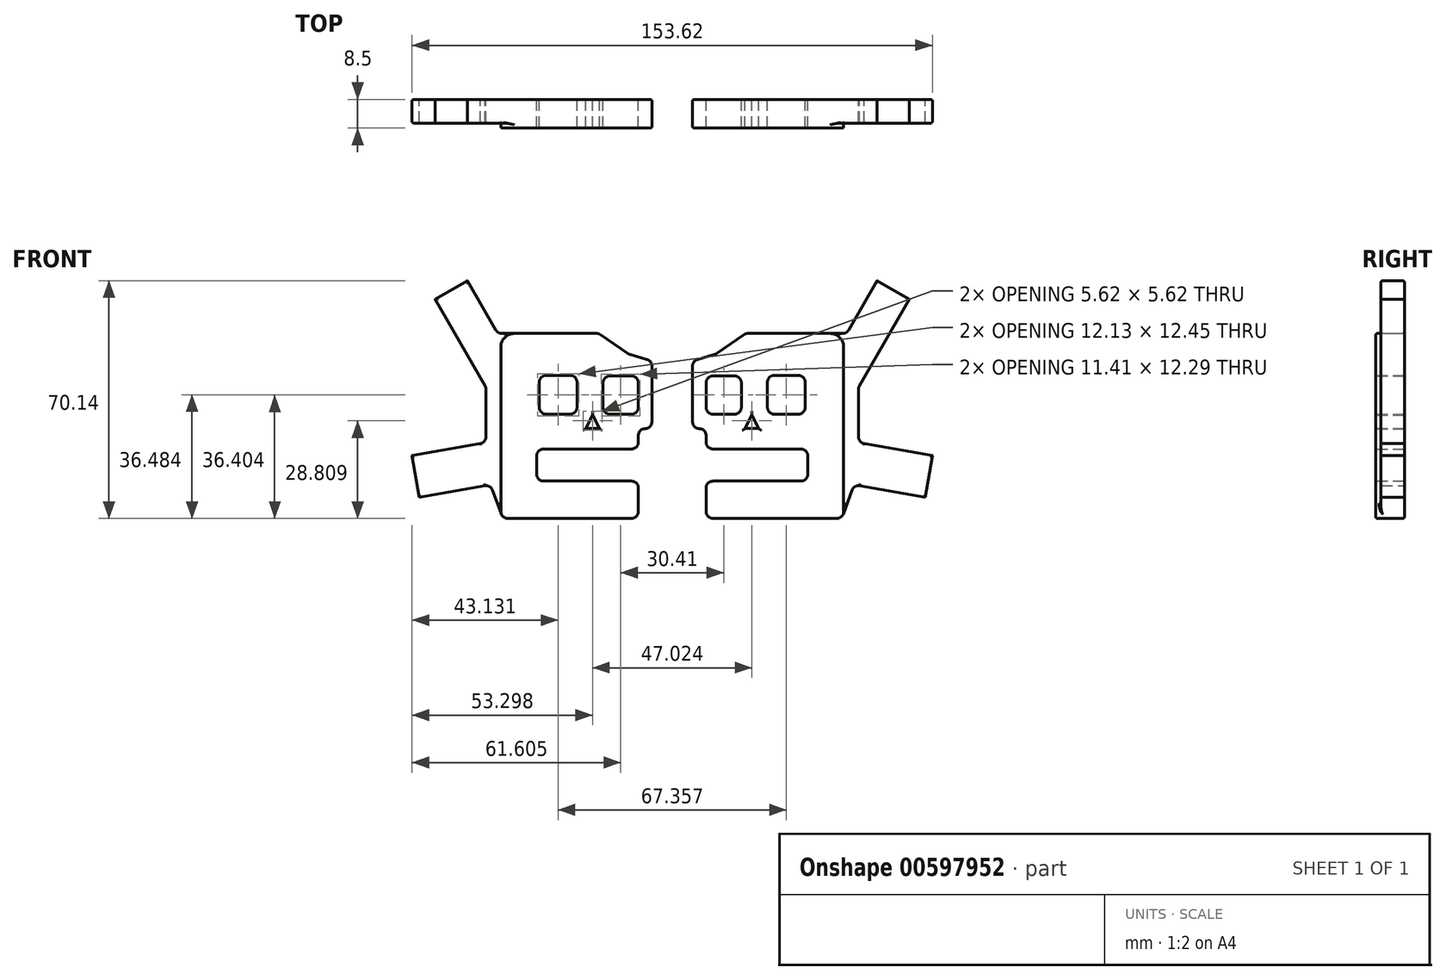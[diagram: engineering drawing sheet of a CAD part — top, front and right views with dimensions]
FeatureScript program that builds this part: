
annotation { "Feature Type Name" : "Feature", "Feature Type Description" : "" }
export const myFeature = defineFeature(function(context is Context, id is Id, definition is map)
    precondition{}
    {
        {
            var Q0;
            Q0=qCreatedBy(makeId("Front.planeOp"),FACE);
            var sketch = newSketch(context, id + "F0", { "sketchPlane" : qUnion([Q0])});
            skLineSegment(sketch, "E0", {"start": v(2, 0) * mm, "end": v(28, 0) * mm});
            skLineSegment(sketch, "E1", {"start": v(30, 2) * mm, "end": v(30, 7.5) * mm});
            skLineSegment(sketch, "E2", {"start": v(28, 9.5) * mm, "end": v(2, 9.5) * mm});
            skPoint(sketch, "E3.visualSharp", {"position": v(30, 9.5) * mm});
            skArc(sketch, "E3.filletArc", {"start": v(30, 7.5) * mm, "mid": v(29.41, 8.91) * mm, "end": v(28, 9.5) * mm});
            skPoint(sketch, "E4.visualSharp", {"position": v(30, 0) * mm});
            skArc(sketch, "E4.filletArc", {"start": v(28, 0) * mm, "mid": v(29.41, 0.59) * mm, "end": v(30, 2) * mm});
            skLineSegment(sketch, "E5", {"start": v(0, -2) * mm, "end": v(0, -9) * mm});
            skLineSegment(sketch, "E6", {"start": v(2, -11) * mm, "end": v(38.6, -11) * mm});
            skLineSegment(sketch, "E7", {"start": v(40.48, -9.68) * mm, "end": v(43.04, -2.66) * mm});
            skLineSegment(sketch, "E8", {"start": v(45, 13.04) * mm, "end": v(45, 27.12) * mm});
            skLineSegment(sketch, "E9", {"start": v(45.27, 28.12) * mm, "end": v(60, 53.64) * mm});
            skLineSegment(sketch, "E10", {"start": v(60, 53.64) * mm, "end": v(50.47, 59.14) * mm});
            skLineSegment(sketch, "E11", {"start": v(50.47, 59.14) * mm, "end": v(42.06, 44.57) * mm});
            skLineSegment(sketch, "E12", {"start": v(40.33, 43.57) * mm, "end": v(12.31, 43.57) * mm});
            skLineSegment(sketch, "E13", {"start": v(11.18, 43.22) * mm, "end": v(3.06, 37.63) * mm});
            skLineSegment(sketch, "E14", {"start": v(2.48, 37.35) * mm, "end": v(-2.55, 35.9) * mm});
            skLineSegment(sketch, "E15", {"start": v(-4, 33.98) * mm, "end": v(-4, 17.49) * mm});
            skLineSegment(sketch, "E16", {"start": v(-2, 15.49) * mm, "end": v(-2, 15.49) * mm});
            skPoint(sketch, "E17.end.orphan", {"position": v(0.1, 9.49) * mm});
            skLineSegment(sketch, "E18", {"start": v(0, 11.5) * mm, "end": v(0, 13.49) * mm});
            skPoint(sketch, "E19.orphan", {"position": v(0.1, 15.49) * mm});
            skLineSegment(sketch, "E20.bottom", {"start": v(2, 19.76) * mm, "end": v(8.41, 19.76) * mm});
            skLineSegment(sketch, "E20.top", {"start": v(2, 31.05) * mm, "end": v(8.41, 31.05) * mm});
            skLineSegment(sketch, "E20.left", {"start": v(0, 21.76) * mm, "end": v(0, 29.05) * mm});
            skLineSegment(sketch, "E20.right", {"start": v(10.41, 21.76) * mm, "end": v(10.41, 29.05) * mm});
            skLineSegment(sketch, "E21.bottom", {"start": v(20.12, 19.76) * mm, "end": v(27.24, 19.76) * mm});
            skLineSegment(sketch, "E21.top", {"start": v(20.12, 31.21) * mm, "end": v(27.24, 31.21) * mm});
            skLineSegment(sketch, "E21.left", {"start": v(18.12, 21.76) * mm, "end": v(18.12, 29.21) * mm});
            skLineSegment(sketch, "E21.right", {"start": v(29.24, 21.76) * mm, "end": v(29.24, 29.21) * mm});
            skLineSegment(sketch, "E22", {"start": v(13.48, 19.5) * mm, "end": v(11.5, 15.5) * mm});
            skLineSegment(sketch, "E23", {"start": v(11.5, 15.5) * mm, "end": v(15.5, 15.5) * mm});
            skLineSegment(sketch, "E24", {"start": v(15.5, 15.5) * mm, "end": v(13.48, 19.5) * mm});
            skPoint(sketch, "E25.visualSharp", {"position": v(29.24, 19.76) * mm});
            skArc(sketch, "E25.filletArc", {"start": v(27.24, 19.76) * mm, "mid": v(28.66, 20.34) * mm, "end": v(29.24, 21.76) * mm});
            skPoint(sketch, "E26.visualSharp", {"position": v(18.12, 19.76) * mm});
            skArc(sketch, "E26.filletArc", {"start": v(18.12, 21.76) * mm, "mid": v(18.7, 20.34) * mm, "end": v(20.12, 19.76) * mm});
            skPoint(sketch, "E27.visualSharp", {"position": v(29.24, 31.21) * mm});
            skArc(sketch, "E27.filletArc", {"start": v(29.24, 29.21) * mm, "mid": v(28.66, 30.62) * mm, "end": v(27.24, 31.21) * mm});
            skPoint(sketch, "E28.visualSharp", {"position": v(18.12, 31.21) * mm});
            skArc(sketch, "E28.filletArc", {"start": v(20.12, 31.21) * mm, "mid": v(18.7, 30.62) * mm, "end": v(18.12, 29.21) * mm});
            skPoint(sketch, "E29.visualSharp", {"position": v(10.41, 31.05) * mm});
            skArc(sketch, "E29.filletArc", {"start": v(10.41, 29.05) * mm, "mid": v(9.82, 30.46) * mm, "end": v(8.41, 31.05) * mm});
            skPoint(sketch, "E30.visualSharp", {"position": v(10.41, 19.76) * mm});
            skArc(sketch, "E30.filletArc", {"start": v(8.41, 19.76) * mm, "mid": v(9.82, 20.34) * mm, "end": v(10.41, 21.76) * mm});
            skPoint(sketch, "E31.visualSharp", {"position": v(0, 19.76) * mm});
            skArc(sketch, "E31.filletArc", {"start": v(0, 21.76) * mm, "mid": v(0.59, 20.34) * mm, "end": v(2, 19.76) * mm});
            skPoint(sketch, "E32.visualSharp", {"position": v(0, 31.05) * mm});
            skArc(sketch, "E32.filletArc", {"start": v(2, 31.05) * mm, "mid": v(0.59, 30.46) * mm, "end": v(0, 29.05) * mm});
            skPoint(sketch, "E33.visualSharp", {"position": v(-4, 15.49) * mm});
            skArc(sketch, "E33.filletArc", {"start": v(-4, 17.49) * mm, "mid": v(-3.41, 16.07) * mm, "end": v(-2, 15.49) * mm});
            skPoint(sketch, "E34.visualSharp", {"position": v(0, 15.49) * mm});
            skArc(sketch, "E34.filletArc", {"start": v(0, 13.49) * mm, "mid": v(-0.59, 14.9) * mm, "end": v(-2, 15.49) * mm});
            skPoint(sketch, "E35.visualSharp", {"position": v(-4, 35.49) * mm});
            skArc(sketch, "E35.filletArc", {"start": v(-2.55, 35.9) * mm, "mid": v(-3.6, 35.18) * mm, "end": v(-4, 33.98) * mm});
            skPoint(sketch, "E36.visualSharp", {"position": v(2.8, 37.44) * mm});
            skArc(sketch, "E36.filletArc", {"start": v(2.48, 37.35) * mm, "mid": v(2.78, 37.46) * mm, "end": v(3.06, 37.63) * mm});
            skPoint(sketch, "E37.visualSharp", {"position": v(11.69, 43.57) * mm});
            skArc(sketch, "E37.filletArc", {"start": v(12.31, 43.57) * mm, "mid": v(11.72, 43.48) * mm, "end": v(11.18, 43.22) * mm});
            skPoint(sketch, "E38.visualSharp", {"position": v(41.49, 43.57) * mm});
            skArc(sketch, "E38.filletArc", {"start": v(40.33, 43.57) * mm, "mid": v(41.33, 43.84) * mm, "end": v(42.06, 44.57) * mm});
            skPoint(sketch, "E39.visualSharp", {"position": v(45, 27.66) * mm});
            skArc(sketch, "E39.filletArc", {"start": v(45.27, 28.12) * mm, "mid": v(45.07, 27.64) * mm, "end": v(45, 27.12) * mm});
            skPoint(sketch, "E40.visualSharp", {"position": v(45, 12.8) * mm});
            skArc(sketch, "E40.filletArc", {"start": v(45, 13.04) * mm, "mid": v(45.48, 11.74) * mm, "end": v(46.7, 11.07) * mm});
            skPoint(sketch, "E41.visualSharp", {"position": v(47.97, 10.9) * mm});
            skArc(sketch, "E41.filletArc", {"start": v(45.24, -1.37) * mm, "mid": v(43.9, -1.62) * mm, "end": v(43.04, -2.66) * mm});
            skPoint(sketch, "E42.visualSharp", {"position": v(0, 0) * mm});
            skArc(sketch, "E42.filletArc", {"start": v(2, 0) * mm, "mid": v(0.59, -0.59) * mm, "end": v(0, -2) * mm});
            skPoint(sketch, "E43.visualSharp", {"position": v(0, -11) * mm});
            skArc(sketch, "E43.filletArc", {"start": v(0, -9) * mm, "mid": v(0.59, -10.41) * mm, "end": v(2, -11) * mm});
            skPoint(sketch, "E44.visualSharp", {"position": v(0, 9.5) * mm});
            skArc(sketch, "E44.filletArc", {"start": v(0, 11.5) * mm, "mid": v(0.59, 10.09) * mm, "end": v(2, 9.5) * mm});
            skPoint(sketch, "E45.visualSharp", {"position": v(40, -11) * mm});
            skArc(sketch, "E45.filletArc", {"start": v(38.6, -11) * mm, "mid": v(39.75, -10.64) * mm, "end": v(40.48, -9.68) * mm});
            skPoint(sketch, "E46.start.orphan", {"position": v(65, 12.8) * mm});
            skLineSegment(sketch, "E47", {"start": v(46.7, 11.07) * mm, "end": v(66.81, 7.52) * mm});
            skLineSegment(sketch, "E48", {"start": v(66.81, 7.52) * mm, "end": v(64.64, -4.8) * mm});
            skLineSegment(sketch, "E49", {"start": v(45.24, -1.37) * mm, "end": v(64.64, -4.8) * mm});
            skSolve(sketch);
        }
        {
            var Q0;
            Q0=qSketchRegion(id+"F0",true);
            extrude(context, id + "F1", {"entities" : qUnion([Q0]), "depth" : 7 * mm, "offsetDistance" : 25 * mm});
        }
        {
            var Q0;
            Q0=makeQuery(id+"F1.opExtrude","CAP_FACE",FACE,{"disambiguationData":[OSD([sQuery(id+"F0.wireOp",EDGE,"E0"),sQuery(id+"F0.wireOp",EDGE,"E1"),sQuery(id+"F0.wireOp",EDGE,"E2"),sQuery(id+"F0.wireOp",EDGE,"E3.filletArc"),sQuery(id+"F0.wireOp",EDGE,"E4.filletArc"),sQuery(id+"F0.wireOp",EDGE,"E5"),sQuery(id+"F0.wireOp",EDGE,"E6"),sQuery(id+"F0.wireOp",EDGE,"E7"),sQuery(id+"F0.wireOp",EDGE,"E8"),sQuery(id+"F0.wireOp",EDGE,"E9"),sQuery(id+"F0.wireOp",EDGE,"E10"),sQuery(id+"F0.wireOp",EDGE,"E11"),sQuery(id+"F0.wireOp",EDGE,"E12"),sQuery(id+"F0.wireOp",EDGE,"E13"),sQuery(id+"F0.wireOp",EDGE,"E14"),sQuery(id+"F0.wireOp",EDGE,"E15"),sQuery(id+"F0.wireOp",EDGE,"E18"),sQuery(id+"F0.wireOp",EDGE,"E20.bottom"),sQuery(id+"F0.wireOp",EDGE,"E20.top"),sQuery(id+"F0.wireOp",EDGE,"E20.left"),sQuery(id+"F0.wireOp",EDGE,"E20.right"),sQuery(id+"F0.wireOp",EDGE,"E21.bottom"),sQuery(id+"F0.wireOp",EDGE,"E21.top"),sQuery(id+"F0.wireOp",EDGE,"E21.left"),sQuery(id+"F0.wireOp",EDGE,"E21.right"),sQuery(id+"F0.wireOp",EDGE,"E22"),sQuery(id+"F0.wireOp",EDGE,"E23"),sQuery(id+"F0.wireOp",EDGE,"E24"),sQuery(id+"F0.wireOp",EDGE,"E25.filletArc"),sQuery(id+"F0.wireOp",EDGE,"E26.filletArc"),sQuery(id+"F0.wireOp",EDGE,"E27.filletArc"),sQuery(id+"F0.wireOp",EDGE,"E28.filletArc"),sQuery(id+"F0.wireOp",EDGE,"E29.filletArc"),sQuery(id+"F0.wireOp",EDGE,"E30.filletArc"),sQuery(id+"F0.wireOp",EDGE,"E31.filletArc"),sQuery(id+"F0.wireOp",EDGE,"E32.filletArc"),sQuery(id+"F0.wireOp",EDGE,"E33.filletArc"),sQuery(id+"F0.wireOp",EDGE,"E34.filletArc"),sQuery(id+"F0.wireOp",EDGE,"E35.filletArc"),sQuery(id+"F0.wireOp",EDGE,"E36.filletArc"),sQuery(id+"F0.wireOp",EDGE,"E37.filletArc"),sQuery(id+"F0.wireOp",EDGE,"E38.filletArc"),sQuery(id+"F0.wireOp",EDGE,"E39.filletArc"),sQuery(id+"F0.wireOp",EDGE,"E40.filletArc"),sQuery(id+"F0.wireOp",EDGE,"E41.filletArc"),sQuery(id+"F0.wireOp",EDGE,"E42.filletArc"),sQuery(id+"F0.wireOp",EDGE,"E43.filletArc"),sQuery(id+"F0.wireOp",EDGE,"E44.filletArc"),sQuery(id+"F0.wireOp",EDGE,"E45.filletArc"),sQuery(id+"F0.wireOp",EDGE,"E47"),sQuery(id+"F0.wireOp",EDGE,"E48"),sQuery(id+"F0.wireOp",EDGE,"E49")])],"isStart":false});
            var sketch = newSketch(context, id + "F2", { "sketchPlane" : qUnion([Q0])});
            skLineSegment(sketch, "E50.0", {"start": v(36.6, 43.57) * mm, "end": v(12.31, 43.57) * mm});
            skPoint(sketch, "E51.0", {"position": v(45, 27.12) * mm});
            skArc(sketch, "E52.0", {"start": v(12.31, 43.57) * mm, "mid": v(11.72, 43.48) * mm, "end": v(11.18, 43.22) * mm});
            skLineSegment(sketch, "E53.0", {"start": v(11.18, 43.22) * mm, "end": v(3.06, 37.63) * mm});
            skPoint(sketch, "E54.0", {"position": v(2.48, 37.35) * mm});
            skLineSegment(sketch, "E55.0", {"start": v(2.48, 37.35) * mm, "end": v(-2.55, 35.9) * mm});
            skArc(sketch, "E56.0", {"start": v(2.48, 37.35) * mm, "mid": v(2.78, 37.46) * mm, "end": v(3.06, 37.63) * mm});
            skArc(sketch, "E57.0", {"start": v(-2.55, 35.9) * mm, "mid": v(-3.6, 35.18) * mm, "end": v(-4, 33.98) * mm});
            skLineSegment(sketch, "E58.0", {"start": v(-4, 33.98) * mm, "end": v(-4, 17.49) * mm});
            skLineSegment(sketch, "E59.0", {"start": v(0, 21.76) * mm, "end": v(0, 29.05) * mm});
            skArc(sketch, "E60.0", {"start": v(2, 31.05) * mm, "mid": v(0.59, 30.46) * mm, "end": v(0, 29.05) * mm});
            skLineSegment(sketch, "E61.0", {"start": v(2, 31.05) * mm, "end": v(8.41, 31.05) * mm});
            skArc(sketch, "E62.0", {"start": v(10.41, 29.05) * mm, "mid": v(9.82, 30.46) * mm, "end": v(8.41, 31.05) * mm});
            skLineSegment(sketch, "E63.0", {"start": v(10.41, 21.76) * mm, "end": v(10.41, 29.05) * mm});
            skArc(sketch, "E64.0", {"start": v(8.41, 19.76) * mm, "mid": v(9.82, 20.34) * mm, "end": v(10.41, 21.76) * mm});
            skLineSegment(sketch, "E65.0", {"start": v(2, 19.76) * mm, "end": v(8.41, 19.76) * mm});
            skArc(sketch, "E66.0", {"start": v(0, 21.76) * mm, "mid": v(0.59, 20.34) * mm, "end": v(2, 19.76) * mm});
            skPoint(sketch, "E67.0", {"position": v(-2, 15.49) * mm});
            skArc(sketch, "E68.0", {"start": v(-4, 17.49) * mm, "mid": v(-3.41, 16.07) * mm, "end": v(-2, 15.49) * mm});
            skPoint(sketch, "E69.0", {"position": v(0, 13.49) * mm});
            skArc(sketch, "E70.0", {"start": v(0, 13.49) * mm, "mid": v(-0.59, 14.9) * mm, "end": v(-2, 15.49) * mm});
            skPoint(sketch, "E71.0", {"position": v(0, 11.5) * mm});
            skLineSegment(sketch, "E72.0", {"start": v(0, 11.5) * mm, "end": v(0, 13.49) * mm});
            skArc(sketch, "E73.0", {"start": v(0, 11.5) * mm, "mid": v(0.59, 10.09) * mm, "end": v(2, 9.5) * mm});
            skLineSegment(sketch, "E74.0", {"start": v(28, 9.5) * mm, "end": v(2, 9.5) * mm});
            skPoint(sketch, "E75.0", {"position": v(13.48, 19.5) * mm});
            skLineSegment(sketch, "E76.0", {"start": v(20.12, 19.76) * mm, "end": v(27.24, 19.76) * mm});
            skPoint(sketch, "E77.0", {"position": v(18.12, 21.76) * mm});
            skLineSegment(sketch, "E78.0", {"start": v(20.12, 31.21) * mm, "end": v(27.24, 31.21) * mm});
            skLineSegment(sketch, "E79.0", {"start": v(29.24, 21.76) * mm, "end": v(29.24, 29.21) * mm});
            skArc(sketch, "E80.0", {"start": v(29.24, 29.21) * mm, "mid": v(28.66, 30.62) * mm, "end": v(27.24, 31.21) * mm});
            skLineSegment(sketch, "E81.0", {"start": v(18.12, 21.76) * mm, "end": v(18.12, 29.21) * mm});
            skArc(sketch, "E82.0", {"start": v(18.12, 21.76) * mm, "mid": v(18.7, 20.34) * mm, "end": v(20.12, 19.76) * mm});
            skArc(sketch, "E83.0", {"start": v(20.12, 31.21) * mm, "mid": v(18.7, 30.62) * mm, "end": v(18.12, 29.21) * mm});
            skArc(sketch, "E84.0", {"start": v(27.24, 19.76) * mm, "mid": v(28.66, 20.34) * mm, "end": v(29.24, 21.76) * mm});
            skLineSegment(sketch, "E85.0", {"start": v(15.5, 15.5) * mm, "end": v(13.48, 19.5) * mm});
            skLineSegment(sketch, "E86.1", {"start": v(13.48, 19.5) * mm, "end": v(11.5, 15.5) * mm});
            skLineSegment(sketch, "E87.0", {"start": v(11.5, 15.5) * mm, "end": v(15.5, 15.5) * mm});
            skArc(sketch, "E88.0", {"start": v(30, 7.5) * mm, "mid": v(29.41, 8.91) * mm, "end": v(28, 9.5) * mm});
            skLineSegment(sketch, "E89.1", {"start": v(30, 2) * mm, "end": v(30, 7.5) * mm});
            skPoint(sketch, "E90.0", {"position": v(28, 0) * mm});
            skLineSegment(sketch, "E91.0", {"start": v(2, 0) * mm, "end": v(28, 0) * mm});
            skArc(sketch, "E92.0", {"start": v(28, 0) * mm, "mid": v(29.41, 0.59) * mm, "end": v(30, 2) * mm});
            skLineSegment(sketch, "E93.0", {"start": v(0, -2) * mm, "end": v(0, -9) * mm});
            skArc(sketch, "E94.0", {"start": v(2, 0) * mm, "mid": v(0.59, -0.59) * mm, "end": v(0, -2) * mm});
            skArc(sketch, "E95.0", {"start": v(0, -9) * mm, "mid": v(0.59, -10.41) * mm, "end": v(2, -11) * mm});
            skLineSegment(sketch, "E96.0", {"start": v(2, -11) * mm, "end": v(38.6, -11) * mm});
            skArc(sketch, "E97.0", {"start": v(38.6, -11) * mm, "mid": v(40.01, -10.41) * mm, "end": v(40.6, -9) * mm});
            skPoint(sketch, "E98.orphan", {"position": v(40.48, -9.68) * mm});
            skLineSegment(sketch, "E99", {"start": v(40.6, -9) * mm, "end": v(40.6, 39.57) * mm});
            skPoint(sketch, "E100.orphan", {"position": v(40.33, 43.57) * mm});
            skPoint(sketch, "E101.visualSharp", {"position": v(40.6, 43.57) * mm});
            skArc(sketch, "E101.filletArc", {"start": v(40.6, 39.57) * mm, "mid": v(39.43, 42.4) * mm, "end": v(36.6, 43.57) * mm});
            skSolve(sketch);
        }
        {
            var Q0;
            Q0=makeQuery(id+"F2.imprint","IMPRINT",FACE,{"disambiguationData":[TD([[makeQuery(id+"F2.imprint","IMPRINT",EDGE,{"derivedFrom":sQuery(id+"F2.wireOp",EDGE,"E50.0")}),1.0]])]});
            extrude(context, id + "F3", {"entities" : qUnion([Q0]), "operationType" : NewBodyOperationType.ADD, "depth" : 1.5 * mm, "offsetDistance" : 25 * mm});
        }
        {
            var Q0;
            Q0=makeQuery(id+"F3.opExtrude","CAP_FACE",FACE,{"disambiguationData":[OSD([sQuery(id+"F2.wireOp",EDGE,"E50.0"),sQuery(id+"F2.wireOp",EDGE,"E52.0"),sQuery(id+"F2.wireOp",EDGE,"E53.0"),sQuery(id+"F2.wireOp",EDGE,"E55.0"),sQuery(id+"F2.wireOp",EDGE,"E56.0"),sQuery(id+"F2.wireOp",EDGE,"E57.0"),sQuery(id+"F2.wireOp",EDGE,"E58.0"),sQuery(id+"F2.wireOp",EDGE,"E59.0"),sQuery(id+"F2.wireOp",EDGE,"E60.0"),sQuery(id+"F2.wireOp",EDGE,"E61.0"),sQuery(id+"F2.wireOp",EDGE,"E62.0"),sQuery(id+"F2.wireOp",EDGE,"E63.0"),sQuery(id+"F2.wireOp",EDGE,"E64.0"),sQuery(id+"F2.wireOp",EDGE,"E65.0"),sQuery(id+"F2.wireOp",EDGE,"E66.0"),sQuery(id+"F2.wireOp",EDGE,"E68.0"),sQuery(id+"F2.wireOp",EDGE,"E70.0"),sQuery(id+"F2.wireOp",EDGE,"E72.0"),sQuery(id+"F2.wireOp",EDGE,"E73.0"),sQuery(id+"F2.wireOp",EDGE,"E74.0"),sQuery(id+"F2.wireOp",EDGE,"E76.0"),sQuery(id+"F2.wireOp",EDGE,"E78.0"),sQuery(id+"F2.wireOp",EDGE,"E79.0"),sQuery(id+"F2.wireOp",EDGE,"E80.0"),sQuery(id+"F2.wireOp",EDGE,"E81.0"),sQuery(id+"F2.wireOp",EDGE,"E82.0"),sQuery(id+"F2.wireOp",EDGE,"E83.0"),sQuery(id+"F2.wireOp",EDGE,"E84.0"),sQuery(id+"F2.wireOp",EDGE,"E85.0"),sQuery(id+"F2.wireOp",EDGE,"E86.1"),sQuery(id+"F2.wireOp",EDGE,"E87.0"),sQuery(id+"F2.wireOp",EDGE,"E88.0"),sQuery(id+"F2.wireOp",EDGE,"E89.1"),sQuery(id+"F2.wireOp",EDGE,"E91.0"),sQuery(id+"F2.wireOp",EDGE,"E92.0"),sQuery(id+"F2.wireOp",EDGE,"E93.0"),sQuery(id+"F2.wireOp",EDGE,"E94.0"),sQuery(id+"F2.wireOp",EDGE,"E95.0"),sQuery(id+"F2.wireOp",EDGE,"E96.0"),sQuery(id+"F2.wireOp",EDGE,"E97.0"),sQuery(id+"F2.wireOp",EDGE,"E99"),sQuery(id+"F2.wireOp",EDGE,"E101.filletArc")])],"isStart":false});
            var Q1;
            Q1=makeQuery(id+"F1.opExtrude","CAP_FACE",FACE,{"disambiguationData":[OSD([sQuery(id+"F0.wireOp",EDGE,"E0"),sQuery(id+"F0.wireOp",EDGE,"E1"),sQuery(id+"F0.wireOp",EDGE,"E2"),sQuery(id+"F0.wireOp",EDGE,"E3.filletArc"),sQuery(id+"F0.wireOp",EDGE,"E4.filletArc"),sQuery(id+"F0.wireOp",EDGE,"E5"),sQuery(id+"F0.wireOp",EDGE,"E6"),sQuery(id+"F0.wireOp",EDGE,"E7"),sQuery(id+"F0.wireOp",EDGE,"E8"),sQuery(id+"F0.wireOp",EDGE,"E9"),sQuery(id+"F0.wireOp",EDGE,"E10"),sQuery(id+"F0.wireOp",EDGE,"E11"),sQuery(id+"F0.wireOp",EDGE,"E12"),sQuery(id+"F0.wireOp",EDGE,"E13"),sQuery(id+"F0.wireOp",EDGE,"E14"),sQuery(id+"F0.wireOp",EDGE,"E15"),sQuery(id+"F0.wireOp",EDGE,"E18"),sQuery(id+"F0.wireOp",EDGE,"E20.bottom"),sQuery(id+"F0.wireOp",EDGE,"E20.top"),sQuery(id+"F0.wireOp",EDGE,"E20.left"),sQuery(id+"F0.wireOp",EDGE,"E20.right"),sQuery(id+"F0.wireOp",EDGE,"E21.bottom"),sQuery(id+"F0.wireOp",EDGE,"E21.top"),sQuery(id+"F0.wireOp",EDGE,"E21.left"),sQuery(id+"F0.wireOp",EDGE,"E21.right"),sQuery(id+"F0.wireOp",EDGE,"E22"),sQuery(id+"F0.wireOp",EDGE,"E23"),sQuery(id+"F0.wireOp",EDGE,"E24"),sQuery(id+"F0.wireOp",EDGE,"E25.filletArc"),sQuery(id+"F0.wireOp",EDGE,"E26.filletArc"),sQuery(id+"F0.wireOp",EDGE,"E27.filletArc"),sQuery(id+"F0.wireOp",EDGE,"E28.filletArc"),sQuery(id+"F0.wireOp",EDGE,"E29.filletArc"),sQuery(id+"F0.wireOp",EDGE,"E30.filletArc"),sQuery(id+"F0.wireOp",EDGE,"E31.filletArc"),sQuery(id+"F0.wireOp",EDGE,"E32.filletArc"),sQuery(id+"F0.wireOp",EDGE,"E33.filletArc"),sQuery(id+"F0.wireOp",EDGE,"E34.filletArc"),sQuery(id+"F0.wireOp",EDGE,"E35.filletArc"),sQuery(id+"F0.wireOp",EDGE,"E36.filletArc"),sQuery(id+"F0.wireOp",EDGE,"E37.filletArc"),sQuery(id+"F0.wireOp",EDGE,"E38.filletArc"),sQuery(id+"F0.wireOp",EDGE,"E39.filletArc"),sQuery(id+"F0.wireOp",EDGE,"E40.filletArc"),sQuery(id+"F0.wireOp",EDGE,"E41.filletArc"),sQuery(id+"F0.wireOp",EDGE,"E42.filletArc"),sQuery(id+"F0.wireOp",EDGE,"E43.filletArc"),sQuery(id+"F0.wireOp",EDGE,"E44.filletArc"),sQuery(id+"F0.wireOp",EDGE,"E45.filletArc"),sQuery(id+"F0.wireOp",EDGE,"E47"),sQuery(id+"F0.wireOp",EDGE,"E48"),sQuery(id+"F0.wireOp",EDGE,"E49")])],"isStart":true});
            var Q2;
            Q2=makeQuery(id+"F1.opExtrude","CAP_FACE",FACE,{"disambiguationData":[OSD([sQuery(id+"F0.wireOp",EDGE,"E0"),sQuery(id+"F0.wireOp",EDGE,"E1"),sQuery(id+"F0.wireOp",EDGE,"E2"),sQuery(id+"F0.wireOp",EDGE,"E3.filletArc"),sQuery(id+"F0.wireOp",EDGE,"E4.filletArc"),sQuery(id+"F0.wireOp",EDGE,"E5"),sQuery(id+"F0.wireOp",EDGE,"E6"),sQuery(id+"F0.wireOp",EDGE,"E7"),sQuery(id+"F0.wireOp",EDGE,"E8"),sQuery(id+"F0.wireOp",EDGE,"E9"),sQuery(id+"F0.wireOp",EDGE,"E10"),sQuery(id+"F0.wireOp",EDGE,"E11"),sQuery(id+"F0.wireOp",EDGE,"E12"),sQuery(id+"F0.wireOp",EDGE,"E13"),sQuery(id+"F0.wireOp",EDGE,"E14"),sQuery(id+"F0.wireOp",EDGE,"E15"),sQuery(id+"F0.wireOp",EDGE,"E18"),sQuery(id+"F0.wireOp",EDGE,"E20.bottom"),sQuery(id+"F0.wireOp",EDGE,"E20.top"),sQuery(id+"F0.wireOp",EDGE,"E20.left"),sQuery(id+"F0.wireOp",EDGE,"E20.right"),sQuery(id+"F0.wireOp",EDGE,"E21.bottom"),sQuery(id+"F0.wireOp",EDGE,"E21.top"),sQuery(id+"F0.wireOp",EDGE,"E21.left"),sQuery(id+"F0.wireOp",EDGE,"E21.right"),sQuery(id+"F0.wireOp",EDGE,"E22"),sQuery(id+"F0.wireOp",EDGE,"E23"),sQuery(id+"F0.wireOp",EDGE,"E24"),sQuery(id+"F0.wireOp",EDGE,"E25.filletArc"),sQuery(id+"F0.wireOp",EDGE,"E26.filletArc"),sQuery(id+"F0.wireOp",EDGE,"E27.filletArc"),sQuery(id+"F0.wireOp",EDGE,"E28.filletArc"),sQuery(id+"F0.wireOp",EDGE,"E29.filletArc"),sQuery(id+"F0.wireOp",EDGE,"E30.filletArc"),sQuery(id+"F0.wireOp",EDGE,"E31.filletArc"),sQuery(id+"F0.wireOp",EDGE,"E32.filletArc"),sQuery(id+"F0.wireOp",EDGE,"E33.filletArc"),sQuery(id+"F0.wireOp",EDGE,"E34.filletArc"),sQuery(id+"F0.wireOp",EDGE,"E35.filletArc"),sQuery(id+"F0.wireOp",EDGE,"E36.filletArc"),sQuery(id+"F0.wireOp",EDGE,"E37.filletArc"),sQuery(id+"F0.wireOp",EDGE,"E38.filletArc"),sQuery(id+"F0.wireOp",EDGE,"E39.filletArc"),sQuery(id+"F0.wireOp",EDGE,"E40.filletArc"),sQuery(id+"F0.wireOp",EDGE,"E41.filletArc"),sQuery(id+"F0.wireOp",EDGE,"E42.filletArc"),sQuery(id+"F0.wireOp",EDGE,"E43.filletArc"),sQuery(id+"F0.wireOp",EDGE,"E44.filletArc"),sQuery(id+"F0.wireOp",EDGE,"E45.filletArc"),sQuery(id+"F0.wireOp",EDGE,"E47"),sQuery(id+"F0.wireOp",EDGE,"E48"),sQuery(id+"F0.wireOp",EDGE,"E49")])],"isStart":false});
            fillet(context, id + "F4", {"entities" : qUnion([Q0, Q1, Q2]), "radius" : 0.5 * mm, "tangentPropagation" : true, "allowEdgeOverflow" : false});
        }
        {
            var Q0;
            Q0=qCreatedBy(makeId("Right.planeOp"),FACE);
            cPlane(context, id + "F5", {"entities" : qUnion([Q0]), "cplaneType" : CPlaneType.OFFSET, "offset" : 10 * mm, "oppositeDirection" : true, "width" : 150 * mm, "height" : 150 * mm});
        }
        {
            var Q0;
            Q0=makeQuery(id+"F1.opExtrude","SWEPT_BODY",BODY,{"disambiguationData":[OSD([sQuery(id+"F0.wireOp",EDGE,"E0"),sQuery(id+"F0.wireOp",EDGE,"E1"),sQuery(id+"F0.wireOp",EDGE,"E2"),sQuery(id+"F0.wireOp",EDGE,"E3.filletArc"),sQuery(id+"F0.wireOp",EDGE,"E4.filletArc"),sQuery(id+"F0.wireOp",EDGE,"E5"),sQuery(id+"F0.wireOp",EDGE,"E6"),sQuery(id+"F0.wireOp",EDGE,"E7"),sQuery(id+"F0.wireOp",EDGE,"E8"),sQuery(id+"F0.wireOp",EDGE,"E9"),sQuery(id+"F0.wireOp",EDGE,"E10"),sQuery(id+"F0.wireOp",EDGE,"E11"),sQuery(id+"F0.wireOp",EDGE,"E12"),sQuery(id+"F0.wireOp",EDGE,"E13"),sQuery(id+"F0.wireOp",EDGE,"E14"),sQuery(id+"F0.wireOp",EDGE,"E15"),sQuery(id+"F0.wireOp",EDGE,"E18"),sQuery(id+"F0.wireOp",EDGE,"E20.bottom"),sQuery(id+"F0.wireOp",EDGE,"E20.top"),sQuery(id+"F0.wireOp",EDGE,"E20.left"),sQuery(id+"F0.wireOp",EDGE,"E20.right"),sQuery(id+"F0.wireOp",EDGE,"E21.bottom"),sQuery(id+"F0.wireOp",EDGE,"E21.top"),sQuery(id+"F0.wireOp",EDGE,"E21.left"),sQuery(id+"F0.wireOp",EDGE,"E21.right"),sQuery(id+"F0.wireOp",EDGE,"E22"),sQuery(id+"F0.wireOp",EDGE,"E23"),sQuery(id+"F0.wireOp",EDGE,"E24"),sQuery(id+"F0.wireOp",EDGE,"E25.filletArc"),sQuery(id+"F0.wireOp",EDGE,"E26.filletArc"),sQuery(id+"F0.wireOp",EDGE,"E27.filletArc"),sQuery(id+"F0.wireOp",EDGE,"E28.filletArc"),sQuery(id+"F0.wireOp",EDGE,"E29.filletArc"),sQuery(id+"F0.wireOp",EDGE,"E30.filletArc"),sQuery(id+"F0.wireOp",EDGE,"E31.filletArc"),sQuery(id+"F0.wireOp",EDGE,"E32.filletArc"),sQuery(id+"F0.wireOp",EDGE,"E33.filletArc"),sQuery(id+"F0.wireOp",EDGE,"E34.filletArc"),sQuery(id+"F0.wireOp",EDGE,"E35.filletArc"),sQuery(id+"F0.wireOp",EDGE,"E36.filletArc"),sQuery(id+"F0.wireOp",EDGE,"E37.filletArc"),sQuery(id+"F0.wireOp",EDGE,"E38.filletArc"),sQuery(id+"F0.wireOp",EDGE,"E39.filletArc"),sQuery(id+"F0.wireOp",EDGE,"E40.filletArc"),sQuery(id+"F0.wireOp",EDGE,"E41.filletArc"),sQuery(id+"F0.wireOp",EDGE,"E42.filletArc"),sQuery(id+"F0.wireOp",EDGE,"E43.filletArc"),sQuery(id+"F0.wireOp",EDGE,"E44.filletArc"),sQuery(id+"F0.wireOp",EDGE,"E45.filletArc"),sQuery(id+"F0.wireOp",EDGE,"E47"),sQuery(id+"F0.wireOp",EDGE,"E48"),sQuery(id+"F0.wireOp",EDGE,"E49")])]});
            var Q1;
            Q1=qCreatedBy(id+"F5.planeOp",FACE);
            mirror(context, id + "F6", {"entities" : qUnion([Q0]), "mirrorPlane" : qUnion([Q1])});
        }
    });
